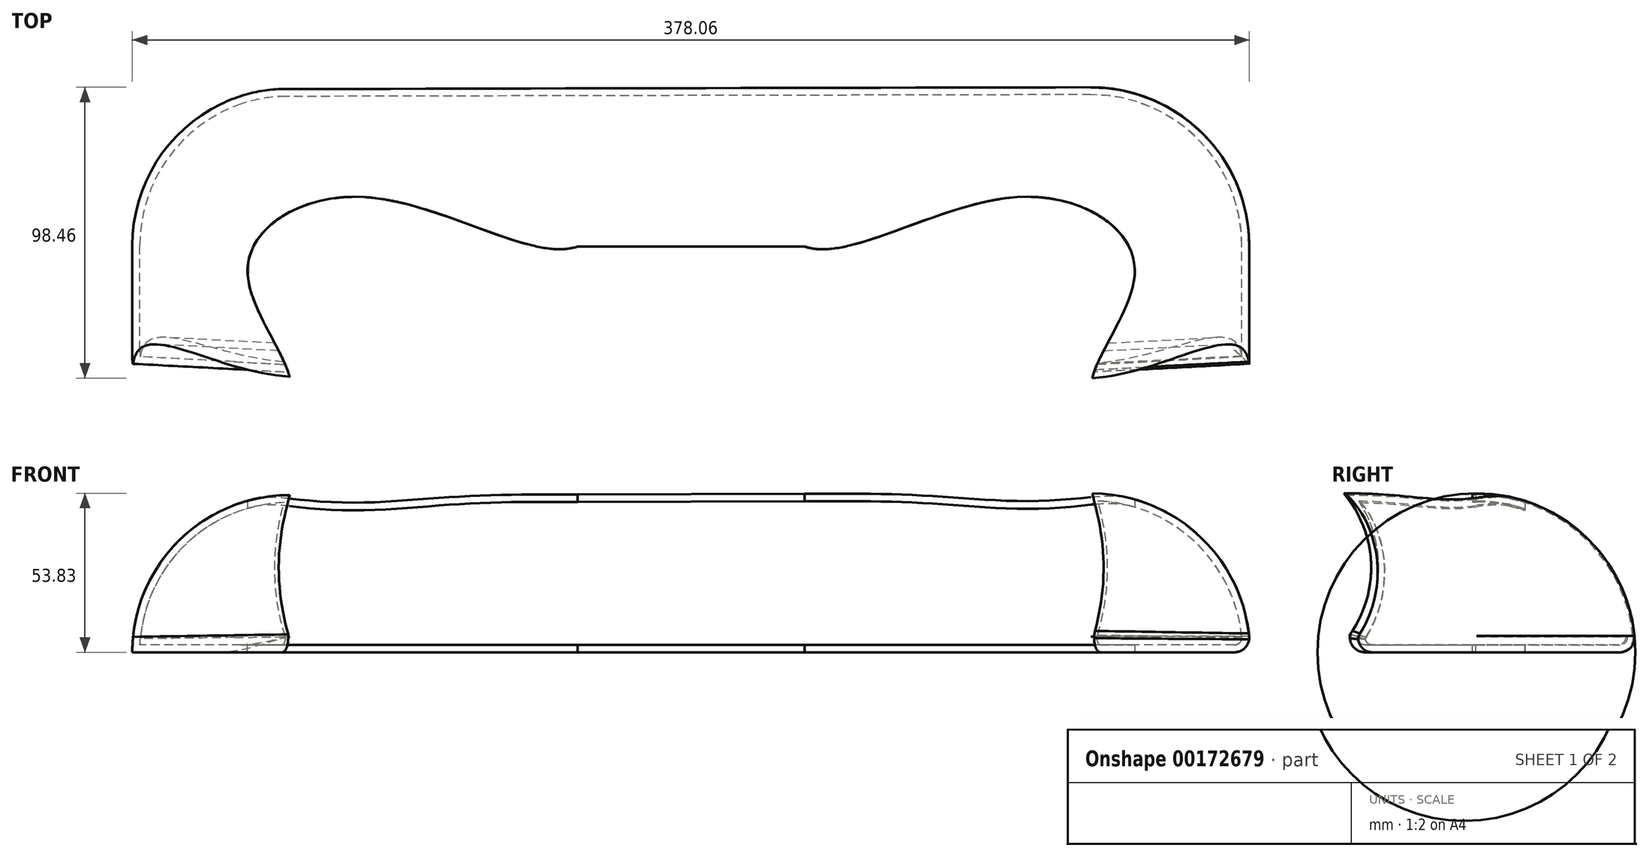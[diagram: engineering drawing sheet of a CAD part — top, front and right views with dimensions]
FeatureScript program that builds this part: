
annotation { "Feature Type Name" : "Feature", "Feature Type Description" : "" }
export const myFeature = defineFeature(function(context is Context, id is Id, definition is map)
    precondition{}
    {
        {
            var Q0;
            Q0=qCreatedBy(makeId("Front.planeOp"),FACE);
            cPlane(context, id + "F0", {"entities" : qUnion([Q0]), "cplaneType" : CPlaneType.OFFSET, "offset" : 60.04 * mm, "width" : 150 * mm, "height" : 150 * mm});
        }
        {
            var Q0;
            Q0=qCreatedBy(id+"F0.planeOp",FACE);
            var sketch = newSketch(context, id + "F1", { "sketchPlane" : qUnion([Q0])});
            skLineSegment(sketch, "E0", {"start": v(189.16, 0) * mm, "end": v(-189.16, 0) * mm});
            skArc(sketch, "E1", {"start": v(-135.93, 53.23) * mm, "mid": v(-173.57, 37.64) * mm, "end": v(-189.16, 0) * mm});
            skArc(sketch, "E2", {"start": v(189.16, 0) * mm, "mid": v(173.4, 38.06) * mm, "end": v(135.33, 53.83) * mm});
            skLineSegment(sketch, "E3", {"start": v(-135.93, 53.23) * mm, "end": v(135.33, 53.83) * mm});
            skSolve(sketch);
        }
        {
            var Q0;
            Q0 = qSketchRegion(id + "F1", true);
            var Q1;
            Q1=sQuery(id+"F1.wireOp",EDGE,"E0");
            revolve(context, id + "F2", {"entities" : qUnion([Q0]), "axis" : qUnion([Q1]), "revolveType" : RevolveType.ONE_DIRECTION, "angle" : 90 * degree});
        }
        {
            var Q0;
            Q0=makeQuery(id+"F2.opRevolve","CAP_FACE",FACE,{"disambiguationData":[OSD([sQuery(id+"F1.wireOp",EDGE,"E0"),sQuery(id+"F1.wireOp",EDGE,"E1"),sQuery(id+"F1.wireOp",EDGE,"E2"),sQuery(id+"F1.wireOp",EDGE,"E3")])],"isStart":true});
            extrude(context, id + "F3", {"entities" : qUnion([Q0]), "operationType" : NewBodyOperationType.ADD, "depth" : 50 * mm});
        }
        {
            var Q0;
            Q0=qCreatedBy(makeId("Top.planeOp"),FACE);
            var sketch = newSketch(context, id + "F4", { "sketchPlane" : qUnion([Q0])});
            skFitSpline(sketch, "E4", {"points": [v(135.33, -110.04) * mm, v(150.16, -68.16) * mm, v(111.06, -43.62) * mm, v(38.43, -60.39) * mm], "startDerivative": vector(-14.92, 102.87) * mm, "endDerivative": vector(-119.7, 42.24) * mm});
            skLineSegment(sketch, "E5", {"start": v(38.43, -60.39) * mm, "end": v(0, -60.39) * mm});
            skFitSpline(sketch, "E6.MirrorCS", {"points": [v(-135.33, -110.04) * mm, v(-150.16, -68.16) * mm, v(-111.06, -43.62) * mm, v(-38.43, -60.39) * mm], "startDerivative": vector(14.92, 102.87) * mm, "endDerivative": vector(119.7, 42.24) * mm});
            skLineSegment(sketch, "E7.MirrorCS", {"start": v(-38.43, -60.39) * mm, "end": v(0, -60.39) * mm});
            skLineSegment(sketch, "E8", {"start": v(-135.33, -110.04) * mm, "end": v(135.33, -110.04) * mm});
            skSolve(sketch);
        }
        {
            var Q0;
            Q0 = qSketchRegion(id + "F4", true);
            extrude(context, id + "F5", {"entities" : qUnion([Q0]), "operationType" : NewBodyOperationType.REMOVE, "depth" : 60 * mm});
        }
        {
            var Q0;
            Q0=qCreatedBy(makeId("Right.planeOp"),FACE);
            var sketch = newSketch(context, id + "F6", { "sketchPlane" : qUnion([Q0])});
            skArc(sketch, "E9", {"start": v(-108.35, 10.69) * mm, "mid": v(-103, 29.65) * mm, "end": v(-109.57, 48.22) * mm});
            skPoint(sketch, "E10.visualSharp", {"position": v(-110.04, 48.83) * mm});
            skArc(sketch, "E10.filletArc", {"start": v(-109.95, 48.76) * mm, "mid": v(-109.76, 48.5) * mm, "end": v(-109.57, 48.22) * mm});
            skPoint(sketch, "E11.visualSharp", {"position": v(-110.04, 8.36) * mm});
            skArc(sketch, "E11.filletArc", {"start": v(-108.35, 10.69) * mm, "mid": v(-109.61, 7.97) * mm, "end": v(-110, 5) * mm});
            skLineSegment(sketch, "E12", {"start": v(-110, 5) * mm, "end": v(-109.95, 48.76) * mm});
            skSolve(sketch);
        }
        {
            var Q0;
            Q0 = qSketchRegion(id + "F6", true);
            extrude(context, id + "F7", {"entities" : qUnion([Q0]), "operationType" : NewBodyOperationType.REMOVE, "endBound" : BoundingType.SYMMETRIC, "depth" : 400 * mm, "hasDraft" : true, "draftAngle" : 3 * degree, "hasSecondDirection" : true, "secondDirectionOppositeDirection" : true, "secondDirectionDepth" : 25 * mm});
        }
        {
            var Q0;
            {var subQ0=sQuery(id+"F6.wireOp",EDGE,"E12");var subQ1=sQuery(id+"F6.wireOp",EDGE,"E11.filletArc");Q0=makeQuery(id+"F7.boolean.opBoolean","INTERSECT",EDGE,{"derivedFrom":[makeQuery(id+"F7.*.split.splitOp","SPLIT",FACE,{"derivedFrom":makeQuery(id+"F7.opExtrude","SWEPT_FACE",FACE,{"disambiguationData":[OSD([sQuery(id+"F6.wireOp",EDGE,"E9")])]})}),makeQuery(id+"F7.*.split.splitOp","SPLIT",FACE,{"derivedFrom":makeQuery(id+"F7.opExtrude","SWEPT_FACE",FACE,{"disambiguationData":[OSD([subQ0]),TDD([makeQuery(id+"F6.imprint","IMPRINT",EDGE,{"disambiguationData":[TD([[makeQuery(id+"F6.imprint","INTERSECT",VERTEX,{"disambiguationData":[OD(0.0)],"derivedFrom":[subQ1,subQ0]}),-1.0]])],"derivedFrom":subQ0})])]})})]});}
            var Q1;
            {var subQ0=sQuery(id+"F6.wireOp",EDGE,"E12");var subQ1=sQuery(id+"F6.wireOp",EDGE,"E11.filletArc");var subQ2=sQuery(id+"F1.wireOp",EDGE,"E0");Q1=makeQuery(id+"F7.boolean.opBoolean","INTERSECT",EDGE,{"derivedFrom":[makeQuery(id+"F3.boolean.opBoolean","MERGE",FACE,{"derivedFrom":[makeQuery(id+"F2.opRevolve","CAP_FACE",FACE,{"disambiguationData":[OSD([subQ2,sQuery(id+"F1.wireOp",EDGE,"E1"),sQuery(id+"F1.wireOp",EDGE,"E2"),sQuery(id+"F1.wireOp",EDGE,"E3")])],"isStart":false}),makeQuery(id+"F3.opExtrude","SWEPT_FACE",FACE,{"disambiguationData":[OSD([subQ2])]})]}),makeQuery(id+"F7.*.split.splitOp","SPLIT",FACE,{"derivedFrom":makeQuery(id+"F7.opExtrude","SWEPT_FACE",FACE,{"disambiguationData":[OSD([subQ0]),TDD([makeQuery(id+"F6.imprint","IMPRINT",EDGE,{"disambiguationData":[TD([[makeQuery(id+"F6.imprint","INTERSECT",VERTEX,{"disambiguationData":[OD(0.0)],"derivedFrom":[subQ1,subQ0]}),-1.0]])],"derivedFrom":subQ0})])]})})]});}
            var Q2;
            {var subQ0=sQuery(id+"F6.wireOp",EDGE,"E12");var subQ1=sQuery(id+"F6.wireOp",EDGE,"E11.filletArc");var subQ2=sQuery(id+"F1.wireOp",EDGE,"E0");Q2=makeQuery(id+"F7.boolean.opBoolean","INTERSECT",EDGE,{"derivedFrom":[makeQuery(id+"F3.boolean.opBoolean","MERGE",FACE,{"derivedFrom":[makeQuery(id+"F2.opRevolve","CAP_FACE",FACE,{"disambiguationData":[OSD([subQ2,sQuery(id+"F1.wireOp",EDGE,"E1"),sQuery(id+"F1.wireOp",EDGE,"E2"),sQuery(id+"F1.wireOp",EDGE,"E3")])],"isStart":false}),makeQuery(id+"F3.opExtrude","SWEPT_FACE",FACE,{"disambiguationData":[OSD([subQ2])]})]}),makeQuery(id+"F7.*.split.splitOp","SPLIT",FACE,{"derivedFrom":makeQuery(id+"F7.opExtrude","SWEPT_FACE",FACE,{"disambiguationData":[OSD([subQ0]),TDD([makeQuery(id+"F6.imprint","IMPRINT",EDGE,{"disambiguationData":[TD([[makeQuery(id+"F6.imprint","INTERSECT",VERTEX,{"disambiguationData":[OD(0.0)],"derivedFrom":[subQ1,subQ0]}),-1.0]])],"derivedFrom":subQ0})])]}),"isFromBackBody":true})]});}
            var Q3;
            Q3=makeQuery(id+"F2.opRevolve","CAP_EDGE",EDGE,{"disambiguationData":[OSD([sQuery(id+"F1.wireOp",EDGE,"E2")])],"isStart":false});
            fillet(context, id + "F8", {"entities" : qUnion([Q0, Q1, Q2, Q3]), "radius" : 5 * mm, "tangentPropagation" : true, "allowEdgeOverflow" : false});
        }
        {
            var Q0;
            Q0=makeQuery(id+"F5.boolean.opBoolean","COPY",FACE,{"derivedFrom":makeQuery(id+"F5.opExtrude","SWEPT_FACE",FACE,{"disambiguationData":[OSD([sQuery(id+"F4.wireOp",EDGE,"E5"),sQuery(id+"F4.wireOp",EDGE,"E7.MirrorCS")])]})});
            var Q1;
            Q1=makeQuery(id+"F5.boolean.opBoolean","COPY",FACE,{"derivedFrom":makeQuery(id+"F5.opExtrude","SWEPT_FACE",FACE,{"disambiguationData":[OSD([sQuery(id+"F4.wireOp",EDGE,"E6.MirrorCS")])]})});
            var Q2;
            Q2=makeQuery(id+"F5.boolean.opBoolean","COPY",FACE,{"derivedFrom":makeQuery(id+"F5.opExtrude","SWEPT_FACE",FACE,{"disambiguationData":[OSD([sQuery(id+"F4.wireOp",EDGE,"E4")])]})});
            shell(context, id + "F9", {"entities" : qUnion([Q0, Q1, Q2]), "thickness" : 2.5 * mm});
        }
    });
